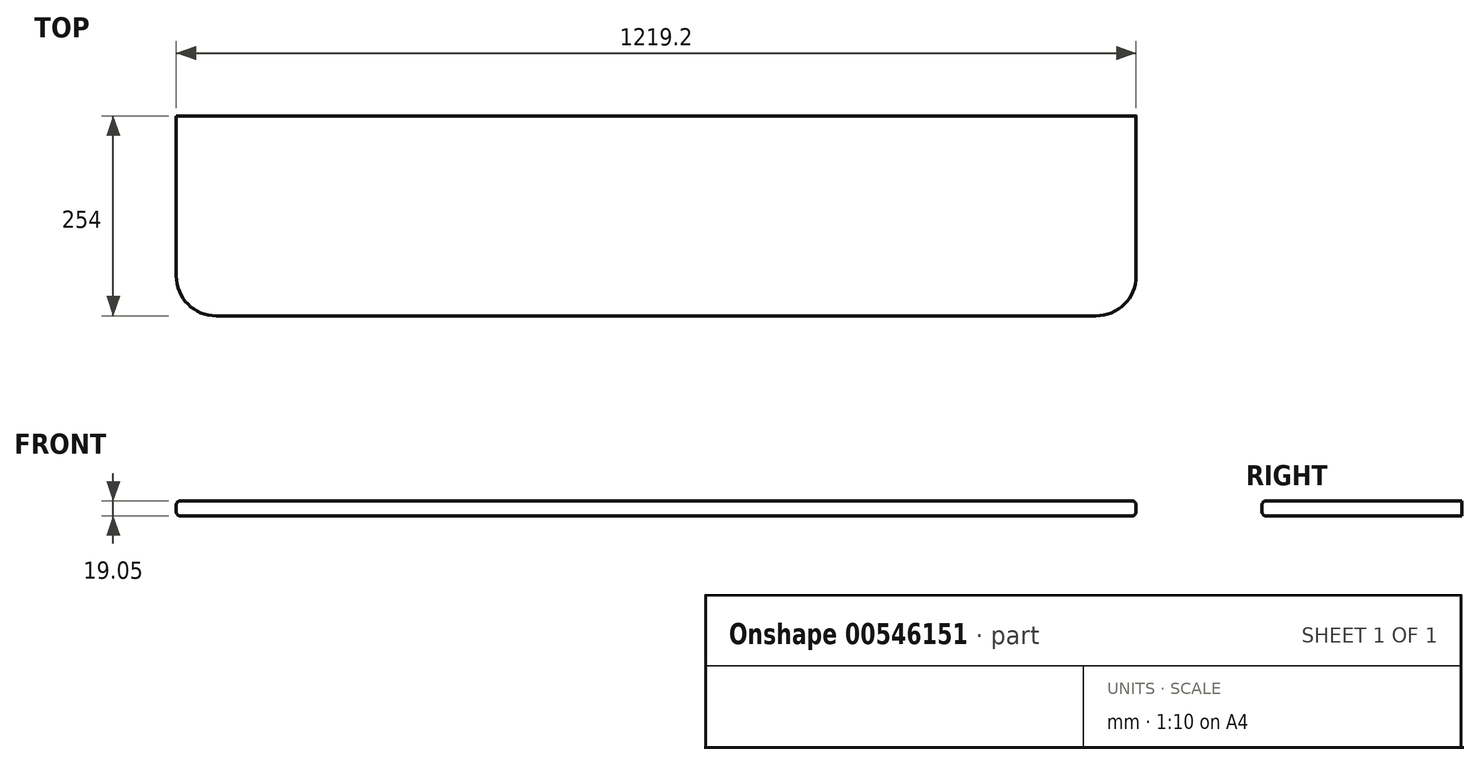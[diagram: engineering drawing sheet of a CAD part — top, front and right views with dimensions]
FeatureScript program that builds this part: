
annotation { "Feature Type Name" : "Feature", "Feature Type Description" : "" }
export const myFeature = defineFeature(function(context is Context, id is Id, definition is map)
    precondition{}
    {
        {
            var Q0;
            Q0=qCreatedBy(makeId("Top.planeOp"),FACE);
            var sketch = newSketch(context, id + "F0", { "sketchPlane" : qUnion([Q0])});
            skLineSegment(sketch, "E0.bottom", {"start": v(558.8, -127) * mm, "end": v(-558.8, -127) * mm});
            skLineSegment(sketch, "E0.top", {"start": v(609.6, 127) * mm, "end": v(-609.6, 127) * mm});
            skLineSegment(sketch, "E0.left", {"start": v(609.6, -76.2) * mm, "end": v(609.6, 127) * mm});
            skLineSegment(sketch, "E0.right", {"start": v(-609.6, -76.2) * mm, "end": v(-609.6, 127) * mm});
            skPoint(sketch, "E0.middle", {"position": v(0, 0) * mm});
            skPoint(sketch, "E1.visualSharp", {"position": v(-609.6, -127) * mm});
            skArc(sketch, "E1.filletArc", {"start": v(-609.6, -76.2) * mm, "mid": v(-594.72, -112.12) * mm, "end": v(-558.8, -127) * mm});
            skPoint(sketch, "E2.visualSharp", {"position": v(609.6, -127) * mm});
            skArc(sketch, "E2.filletArc", {"start": v(558.8, -127) * mm, "mid": v(594.72, -112.12) * mm, "end": v(609.6, -76.2) * mm});
            skSolve(sketch);
        }
        {
            var Q0;
            Q0=makeQuery(id+"F0.imprint","IMPRINT",FACE,{"disambiguationData":[TD([[makeQuery(id+"F0.imprint","IMPRINT",EDGE,{"derivedFrom":sQuery(id+"F0.wireOp",EDGE,"E0.bottom")}),-1.0]])]});
            extrude(context, id + "F1", {"entities" : qUnion([Q0]), "depth" : 19.05 * mm, "offsetDistance" : 25.4 * mm});
        }
        {
            var Q0;
            Q0=makeQuery(id+"F1.opExtrude","CAP_EDGE",EDGE,{"disambiguationData":[OSD([sQuery(id+"F0.wireOp",EDGE,"E0.bottom")])],"isStart":false});
            fillet(context, id + "F2", {"entities" : qUnion([Q0]), "radius" : 5.08 * mm, "tangentPropagation" : true, "allowEdgeOverflow" : false});
        }
        {
            var Q0;
            Q0=makeQuery(id+"F1.opExtrude","CAP_EDGE",EDGE,{"disambiguationData":[OSD([sQuery(id+"F0.wireOp",EDGE,"E0.bottom")])],"isStart":true});
            fillet(context, id + "F3", {"entities" : qUnion([Q0]), "radius" : 5.08 * mm, "tangentPropagation" : true, "allowEdgeOverflow" : false});
        }
    });
